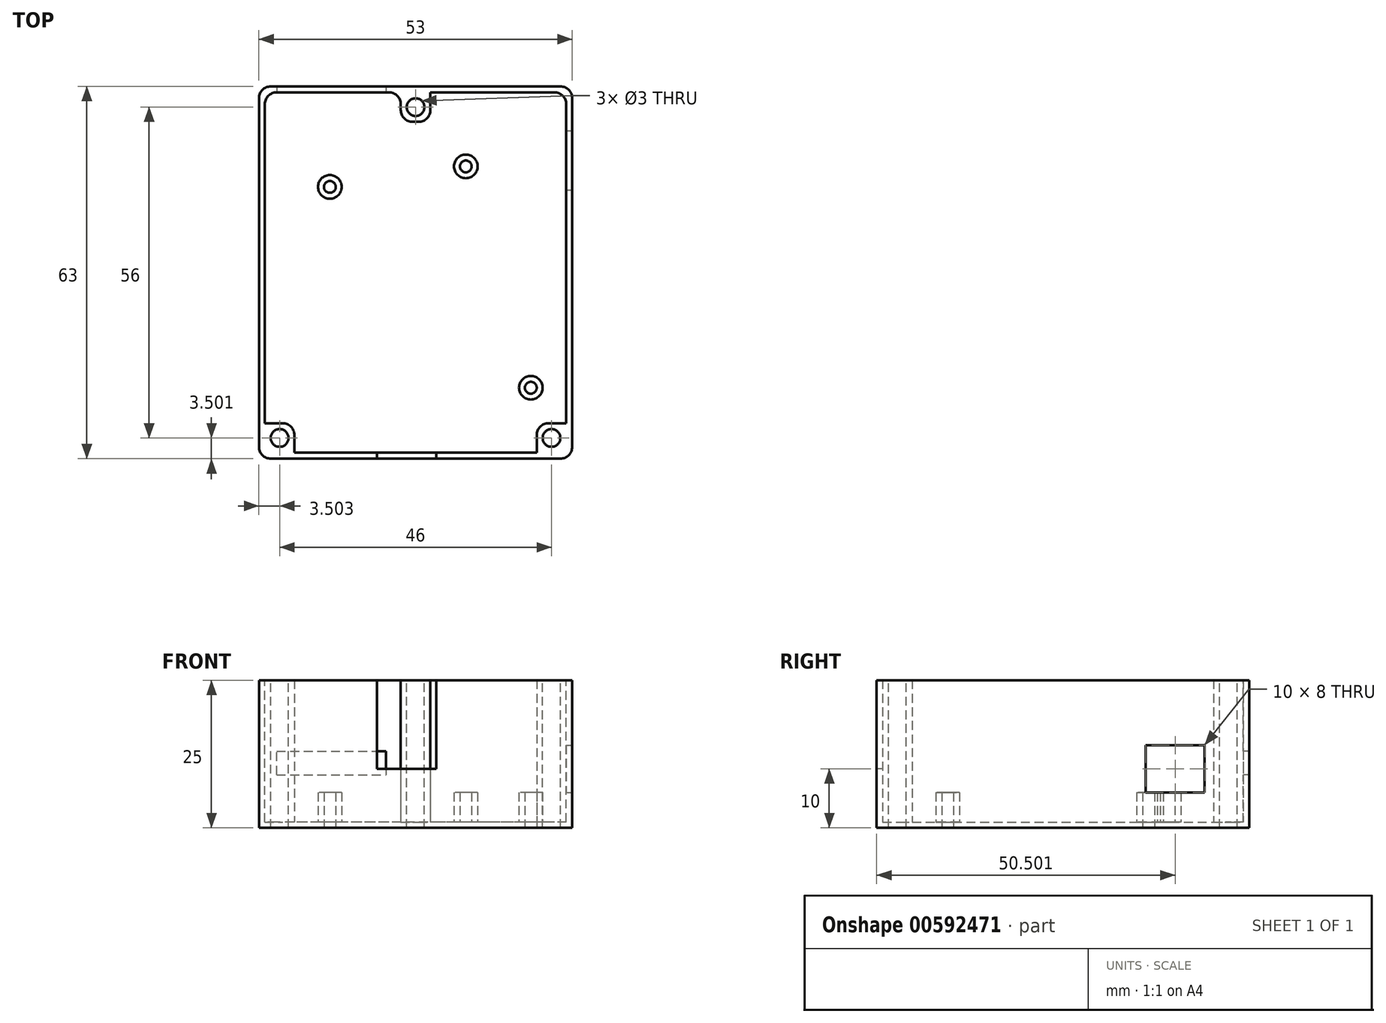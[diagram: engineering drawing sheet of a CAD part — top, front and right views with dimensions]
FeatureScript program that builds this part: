
annotation { "Feature Type Name" : "Feature", "Feature Type Description" : "" }
export const myFeature = defineFeature(function(context is Context, id is Id, definition is map)
    precondition{}
    {
        {
            var Q0;
            Q0=qCreatedBy(makeId("Top.planeOp"),FACE);
            var sketch = newSketch(context, id + "F0", { "sketchPlane" : qUnion([Q0])});
            skLineSegment(sketch, "E0.bottom", {"start": v(-63.44, 80.45) * mm, "end": v(-10.44, 80.45) * mm});
            skLineSegment(sketch, "E0.top", {"start": v(-63.44, 17.45) * mm, "end": v(-10.44, 17.45) * mm});
            skLineSegment(sketch, "E0.left", {"start": v(-63.44, 80.45) * mm, "end": v(-63.44, 17.45) * mm});
            skLineSegment(sketch, "E0.right", {"start": v(-10.44, 80.45) * mm, "end": v(-10.44, 17.45) * mm});
            skSolve(sketch);
        }
        {
            var Q0;
            Q0=makeQuery(id+"F0.imprint","IMPRINT",FACE,{"disambiguationData":[TD([[makeQuery(id+"F0.imprint","IMPRINT",EDGE,{"derivedFrom":sQuery(id+"F0.wireOp",EDGE,"E0.bottom")}),-1.0]])]});
            extrude(context, id + "F1", {"entities" : qUnion([Q0]), "depth" : 25 * mm, "offsetDistance" : 25 * mm});
        }
        {
            var Q0;
            Q0=makeQuery(id+"F1.opExtrude","CAP_FACE",FACE,{"disambiguationData":[OSD([sQuery(id+"F0.wireOp",EDGE,"E0.bottom"),sQuery(id+"F0.wireOp",EDGE,"E0.top"),sQuery(id+"F0.wireOp",EDGE,"E0.left"),sQuery(id+"F0.wireOp",EDGE,"E0.right")])],"isStart":false});
            var sketch = newSketch(context, id + "F2", { "sketchPlane" : qUnion([Q0])});
            skLineSegment(sketch, "E1.bottom", {"start": v(-11.44, 18.45) * mm, "end": v(-62.44, 18.45) * mm});
            skLineSegment(sketch, "E1.top", {"start": v(-11.44, 79.45) * mm, "end": v(-62.44, 79.45) * mm});
            skLineSegment(sketch, "E1.left", {"start": v(-11.44, 18.45) * mm, "end": v(-11.44, 79.45) * mm});
            skLineSegment(sketch, "E1.right", {"start": v(-62.44, 18.45) * mm, "end": v(-62.44, 79.45) * mm});
            skPoint(sketch, "E1.middle", {"position": v(-36.94, 48.95) * mm});
            skPoint(sketch, "E1.middle.positionSnap0", {"position": v(-63.44, 48.95) * mm});
            skPoint(sketch, "E1.middle.positionSnap1", {"position": v(-36.94, 80.45) * mm});
            skPoint(sketch, "E1.centerSnap0", {"position": v(-63.44, 48.95) * mm});
            skPoint(sketch, "E1.centerSnap1", {"position": v(-36.94, 80.45) * mm});
            skSolve(sketch);
        }
        {
            var Q0;
            Q0=makeQuery(id+"F2.imprint","IMPRINT",FACE,{"disambiguationData":[TD([[makeQuery(id+"F2.imprint","IMPRINT",EDGE,{"derivedFrom":sQuery(id+"F2.wireOp",EDGE,"E1.bottom")}),-1.0]])]});
            extrude(context, id + "F3", {"entities" : qUnion([Q0]), "operationType" : NewBodyOperationType.REMOVE, "oppositeDirection" : true, "depth" : 24 * mm, "offsetDistance" : 25 * mm});
        }
        {
            var Q0;
            Q0=makeQuery(id+"F3.boolean.opBoolean","COPY",FACE,{"derivedFrom":makeQuery(id+"F3.opExtrude","CAP_FACE",FACE,{"disambiguationData":[OSD([sQuery(id+"F2.wireOp",EDGE,"E1.bottom"),sQuery(id+"F2.wireOp",EDGE,"E1.top"),sQuery(id+"F2.wireOp",EDGE,"E1.left"),sQuery(id+"F2.wireOp",EDGE,"E1.right")])],"isStart":false})});
            var sketch = newSketch(context, id + "F4", { "sketchPlane" : qUnion([Q0])});
            skLineSegment(sketch, "E2.bottom", {"start": v(-39.44, 79.45) * mm, "end": v(-34.44, 79.45) * mm});
            skLineSegment(sketch, "E2.top", {"start": v(-39.44, 74.45) * mm, "end": v(-34.44, 74.45) * mm});
            skLineSegment(sketch, "E2.left", {"start": v(-39.44, 79.45) * mm, "end": v(-39.44, 74.45) * mm});
            skLineSegment(sketch, "E2.right", {"start": v(-34.44, 79.45) * mm, "end": v(-34.44, 74.45) * mm});
            skLineSegment(sketch, "E3.bottom", {"start": v(-62.44, 18.45) * mm, "end": v(-57.44, 18.45) * mm});
            skLineSegment(sketch, "E3.top", {"start": v(-62.44, 23.45) * mm, "end": v(-57.44, 23.45) * mm});
            skLineSegment(sketch, "E3.left", {"start": v(-62.44, 18.45) * mm, "end": v(-62.44, 23.45) * mm});
            skLineSegment(sketch, "E3.right", {"start": v(-57.44, 18.45) * mm, "end": v(-57.44, 23.45) * mm});
            skLineSegment(sketch, "E4.bottom", {"start": v(-11.44, 18.45) * mm, "end": v(-16.44, 18.45) * mm});
            skLineSegment(sketch, "E4.top", {"start": v(-11.44, 23.45) * mm, "end": v(-16.44, 23.45) * mm});
            skLineSegment(sketch, "E4.left", {"start": v(-11.44, 18.45) * mm, "end": v(-11.44, 23.45) * mm});
            skLineSegment(sketch, "E4.right", {"start": v(-16.44, 18.45) * mm, "end": v(-16.44, 23.45) * mm});
            skSolve(sketch);
        }
        {
            var Q0;
            Q0=makeQuery(id+"F4.imprint","IMPRINT",FACE,{"disambiguationData":[TD([[makeQuery(id+"F4.imprint","IMPRINT",EDGE,{"derivedFrom":sQuery(id+"F4.wireOp",EDGE,"E2.bottom")}),1.0]])]});
            var Q1;
            Q1=makeQuery(id+"F4.imprint","IMPRINT",FACE,{"disambiguationData":[TD([[makeQuery(id+"F4.imprint","IMPRINT",EDGE,{"derivedFrom":sQuery(id+"F4.wireOp",EDGE,"E3.bottom")}),-1.0]])]});
            var Q2;
            Q2=makeQuery(id+"F4.imprint","IMPRINT",FACE,{"disambiguationData":[TD([[makeQuery(id+"F4.imprint","IMPRINT",EDGE,{"derivedFrom":sQuery(id+"F4.wireOp",EDGE,"E4.bottom")}),-1.0]])]});
            extrude(context, id + "F5", {"entities" : qUnion([Q0, Q1, Q2]), "operationType" : NewBodyOperationType.ADD, "depth" : 24 * mm, "offsetDistance" : 25 * mm});
        }
        {
            var Q0;
            Q0=makeQuery(id+"F5.boolean.opBoolean","MERGE",FACE,{"derivedFrom":[makeQuery(id+"F1.opExtrude","CAP_FACE",FACE,{"disambiguationData":[OSD([sQuery(id+"F0.wireOp",EDGE,"E0.bottom"),sQuery(id+"F0.wireOp",EDGE,"E0.top"),sQuery(id+"F0.wireOp",EDGE,"E0.left"),sQuery(id+"F0.wireOp",EDGE,"E0.right")])],"isStart":false}),makeQuery(id+"F5.opExtrude","CAP_FACE",FACE,{"disambiguationData":[OSD([sQuery(id+"F4.wireOp",EDGE,"E2.bottom"),sQuery(id+"F4.wireOp",EDGE,"E2.top"),sQuery(id+"F4.wireOp",EDGE,"E2.left"),sQuery(id+"F4.wireOp",EDGE,"E2.right")])],"isStart":false}),makeQuery(id+"F5.opExtrude","CAP_FACE",FACE,{"disambiguationData":[OSD([sQuery(id+"F4.wireOp",EDGE,"E3.bottom"),sQuery(id+"F4.wireOp",EDGE,"E3.top"),sQuery(id+"F4.wireOp",EDGE,"E3.left"),sQuery(id+"F4.wireOp",EDGE,"E3.right")])],"isStart":false}),makeQuery(id+"F5.opExtrude","CAP_FACE",FACE,{"disambiguationData":[OSD([sQuery(id+"F4.wireOp",EDGE,"E4.bottom"),sQuery(id+"F4.wireOp",EDGE,"E4.top"),sQuery(id+"F4.wireOp",EDGE,"E4.left"),sQuery(id+"F4.wireOp",EDGE,"E4.right")])],"isStart":false})]});
            var sketch = newSketch(context, id + "F6", { "sketchPlane" : qUnion([Q0])});
            skCircle(sketch, "E5", {"center": v(-36.94, 76.95) * mm, "radius": 1.5 * mm});
            skPoint(sketch, "E5.centerSnap0", {"position": v(-39.44, 76.95) * mm});
            skPoint(sketch, "E5.centerSnap1", {"position": v(-36.94, 74.45) * mm});
            skCircle(sketch, "E6", {"center": v(-59.94, 20.95) * mm, "radius": 1.5 * mm});
            skPoint(sketch, "E6.centerSnap0", {"position": v(-57.44, 20.95) * mm});
            skPoint(sketch, "E6.centerSnap1", {"position": v(-59.94, 23.45) * mm});
            skCircle(sketch, "E7", {"center": v(-13.94, 20.95) * mm, "radius": 1.5 * mm});
            skPoint(sketch, "E7.centerSnap0", {"position": v(-13.94, 23.45) * mm});
            skPoint(sketch, "E7.centerSnap1", {"position": v(-16.44, 20.95) * mm});
            skSolve(sketch);
        }
        {
            var Q0;
            Q0=makeQuery(id+"F6.imprint","IMPRINT",FACE,{"disambiguationData":[TD([[makeQuery(id+"F6.imprint","IMPRINT",EDGE,{"derivedFrom":sQuery(id+"F6.wireOp",EDGE,"E5")}),1.0]])]});
            var Q1;
            Q1=makeQuery(id+"F6.imprint","IMPRINT",FACE,{"disambiguationData":[TD([[makeQuery(id+"F6.imprint","IMPRINT",EDGE,{"derivedFrom":sQuery(id+"F6.wireOp",EDGE,"E6")}),1.0]])]});
            var Q2;
            Q2=makeQuery(id+"F6.imprint","IMPRINT",FACE,{"disambiguationData":[TD([[makeQuery(id+"F6.imprint","IMPRINT",EDGE,{"derivedFrom":sQuery(id+"F6.wireOp",EDGE,"E7")}),1.0]])]});
            extrude(context, id + "F7", {"entities" : qUnion([Q0, Q1, Q2]), "operationType" : NewBodyOperationType.REMOVE, "oppositeDirection" : true, "depth" : 15 * mm, "offsetDistance" : 25 * mm});
        }
        {
            var Q0;
            Q0=makeQuery(id+"F3.boolean.opBoolean","COPY",FACE,{"derivedFrom":makeQuery(id+"F3.opExtrude","CAP_FACE",FACE,{"disambiguationData":[OSD([sQuery(id+"F2.wireOp",EDGE,"E1.bottom"),sQuery(id+"F2.wireOp",EDGE,"E1.top"),sQuery(id+"F2.wireOp",EDGE,"E1.left"),sQuery(id+"F2.wireOp",EDGE,"E1.right")])],"isStart":false})});
            var sketch = newSketch(context, id + "F8", { "sketchPlane" : qUnion([Q0])});
            skCircle(sketch, "E8", {"center": v(-51.44, 63.45) * mm, "radius": 2 * mm});
            skCircle(sketch, "E9", {"center": v(-17.44, 29.45) * mm, "radius": 2 * mm});
            skCircle(sketch, "E10", {"center": v(-51.44, 63.45) * mm, "radius": 1 * mm});
            skCircle(sketch, "E11", {"center": v(-17.44, 29.45) * mm, "radius": 1 * mm});
            skSolve(sketch);
        }
        {
            var Q0;
            Q0=makeQuery(id+"F8.imprint","IMPRINT",FACE,{"disambiguationData":[TD([[makeQuery(id+"F8.imprint","IMPRINT",EDGE,{"derivedFrom":sQuery(id+"F8.wireOp",EDGE,"E8")}),1.0]])]});
            var Q1;
            Q1=makeQuery(id+"F8.imprint","IMPRINT",FACE,{"disambiguationData":[TD([[makeQuery(id+"F8.imprint","IMPRINT",EDGE,{"derivedFrom":sQuery(id+"F8.wireOp",EDGE,"E9")}),1.0]])]});
            extrude(context, id + "F9", {"entities" : qUnion([Q0, Q1]), "operationType" : NewBodyOperationType.ADD, "depth" : 5 * mm, "offsetDistance" : 25 * mm});
        }
        {
            var Q0;
            Q0=makeQuery(id+"F9.boolean.opBoolean","SPLIT",FACE,{"disambiguationData":[TD([makeQuery(id+"F9.opExtrude","SWEPT_FACE",FACE,{"disambiguationData":[OSD([sQuery(id+"F8.wireOp",EDGE,"E10")])]})])],"derivedFrom":makeQuery(id+"F3.boolean.opBoolean","COPY",FACE,{"derivedFrom":makeQuery(id+"F3.opExtrude","CAP_FACE",FACE,{"disambiguationData":[OSD([sQuery(id+"F2.wireOp",EDGE,"E1.bottom"),sQuery(id+"F2.wireOp",EDGE,"E1.top"),sQuery(id+"F2.wireOp",EDGE,"E1.left"),sQuery(id+"F2.wireOp",EDGE,"E1.right")])],"isStart":false})})});
            var Q1;
            Q1=makeQuery(id+"F9.boolean.opBoolean","SPLIT",FACE,{"disambiguationData":[TD([makeQuery(id+"F9.opExtrude","SWEPT_FACE",FACE,{"disambiguationData":[OSD([sQuery(id+"F8.wireOp",EDGE,"E11")])]})])],"derivedFrom":makeQuery(id+"F3.boolean.opBoolean","COPY",FACE,{"derivedFrom":makeQuery(id+"F3.opExtrude","CAP_FACE",FACE,{"disambiguationData":[OSD([sQuery(id+"F2.wireOp",EDGE,"E1.bottom"),sQuery(id+"F2.wireOp",EDGE,"E1.top"),sQuery(id+"F2.wireOp",EDGE,"E1.left"),sQuery(id+"F2.wireOp",EDGE,"E1.right")])],"isStart":false})})});
            extrude(context, id + "F10", {"entities" : qUnion([Q0, Q1]), "operationType" : NewBodyOperationType.REMOVE, "oppositeDirection" : true, "depth" : 1 * mm, "offsetDistance" : 25 * mm});
        }
        {
            var Q0;
            Q0=makeQuery(id+"F1.opExtrude","SWEPT_EDGE",EDGE,{"disambiguationData":[OSD([sQuery(id+"F0.wireOp",EDGE,"E0.bottom"),sQuery(id+"F0.wireOp",EDGE,"E0.left")])]});
            var Q1;
            Q1=makeQuery(id+"F1.opExtrude","SWEPT_EDGE",EDGE,{"disambiguationData":[OSD([sQuery(id+"F0.wireOp",EDGE,"E0.bottom"),sQuery(id+"F0.wireOp",EDGE,"E0.right")])]});
            var Q2;
            Q2=makeQuery(id+"F1.opExtrude","SWEPT_EDGE",EDGE,{"disambiguationData":[OSD([sQuery(id+"F0.wireOp",EDGE,"E0.top"),sQuery(id+"F0.wireOp",EDGE,"E0.right")])]});
            var Q3;
            Q3=makeQuery(id+"F1.opExtrude","SWEPT_EDGE",EDGE,{"disambiguationData":[OSD([sQuery(id+"F0.wireOp",EDGE,"E0.top"),sQuery(id+"F0.wireOp",EDGE,"E0.left")])]});
            var Q4;
            Q4=makeQuery(id+"F5.opExtrude","SWEPT_EDGE",EDGE,{"disambiguationData":[OSD([sQuery(id+"F4.wireOp",EDGE,"E2.top"),sQuery(id+"F4.wireOp",EDGE,"E2.left")])]});
            var Q5;
            Q5=makeQuery(id+"F5.opExtrude","SWEPT_EDGE",EDGE,{"disambiguationData":[OSD([sQuery(id+"F4.wireOp",EDGE,"E2.top"),sQuery(id+"F4.wireOp",EDGE,"E2.right")])]});
            var Q6;
            Q6=makeQuery(id+"F5.opExtrude","SWEPT_EDGE",EDGE,{"disambiguationData":[OSD([sQuery(id+"F2.wireOp",EDGE,"E1.top"),sQuery(id+"F4.wireOp",EDGE,"E2.bottom"),sQuery(id+"F4.wireOp",EDGE,"E2.left")])]});
            var Q7;
            Q7=makeQuery(id+"F5.opExtrude","SWEPT_EDGE",EDGE,{"disambiguationData":[OSD([sQuery(id+"F2.wireOp",EDGE,"E1.top"),sQuery(id+"F4.wireOp",EDGE,"E2.bottom"),sQuery(id+"F4.wireOp",EDGE,"E2.right")])]});
            var Q8;
            Q8=makeQuery(id+"F5.opExtrude","SWEPT_EDGE",EDGE,{"disambiguationData":[OSD([sQuery(id+"F2.wireOp",EDGE,"E1.right"),sQuery(id+"F4.wireOp",EDGE,"E3.top"),sQuery(id+"F4.wireOp",EDGE,"E3.left")])]});
            var Q9;
            Q9=makeQuery(id+"F5.opExtrude","SWEPT_EDGE",EDGE,{"disambiguationData":[OSD([sQuery(id+"F2.wireOp",EDGE,"E1.bottom"),sQuery(id+"F4.wireOp",EDGE,"E3.bottom"),sQuery(id+"F4.wireOp",EDGE,"E3.right")])]});
            var Q10;
            Q10=makeQuery(id+"F5.opExtrude","SWEPT_EDGE",EDGE,{"disambiguationData":[OSD([sQuery(id+"F2.wireOp",EDGE,"E1.bottom"),sQuery(id+"F4.wireOp",EDGE,"E4.bottom"),sQuery(id+"F4.wireOp",EDGE,"E4.right")])]});
            var Q11;
            Q11=makeQuery(id+"F5.opExtrude","SWEPT_EDGE",EDGE,{"disambiguationData":[OSD([sQuery(id+"F2.wireOp",EDGE,"E1.left"),sQuery(id+"F4.wireOp",EDGE,"E4.top"),sQuery(id+"F4.wireOp",EDGE,"E4.left")])]});
            fillet(context, id + "F11", {"entities" : qUnion([Q0, Q1, Q2, Q3, Q4, Q5, Q6, Q7, Q8, Q9, Q10, Q11]), "radius" : 2 * mm, "tangentPropagation" : true, "allowEdgeOverflow" : false});
        }
        {
            var Q0;
            Q0=makeQuery(id+"F5.opExtrude","SWEPT_EDGE",EDGE,{"disambiguationData":[OSD([sQuery(id+"F4.wireOp",EDGE,"E3.top"),sQuery(id+"F4.wireOp",EDGE,"E3.right")])]});
            var Q1;
            Q1=makeQuery(id+"F5.opExtrude","SWEPT_EDGE",EDGE,{"disambiguationData":[OSD([sQuery(id+"F4.wireOp",EDGE,"E4.top"),sQuery(id+"F4.wireOp",EDGE,"E4.right")])]});
            fillet(context, id + "F12", {"entities" : qUnion([Q0, Q1]), "radius" : 2 * mm, "tangentPropagation" : true, "allowEdgeOverflow" : false});
        }
        {
            var Q0;
            Q0=makeQuery(id+"F3.boolean.opBoolean","COPY",EDGE,{"derivedFrom":makeQuery(id+"F3.opExtrude","SWEPT_EDGE",EDGE,{"disambiguationData":[OSD([sQuery(id+"F2.wireOp",EDGE,"E1.top"),sQuery(id+"F2.wireOp",EDGE,"E1.right")])]})});
            fillet(context, id + "F13", {"entities" : qUnion([Q0]), "radius" : 2 * mm, "tangentPropagation" : true, "allowEdgeOverflow" : false});
        }
        {
            var Q0;
            Q0=makeQuery(id+"F3.boolean.opBoolean","COPY",EDGE,{"derivedFrom":makeQuery(id+"F3.opExtrude","SWEPT_EDGE",EDGE,{"disambiguationData":[OSD([sQuery(id+"F2.wireOp",EDGE,"E1.top"),sQuery(id+"F2.wireOp",EDGE,"E1.left")])]})});
            fillet(context, id + "F14", {"entities" : qUnion([Q0]), "radius" : 2 * mm, "tangentPropagation" : true, "allowEdgeOverflow" : false});
        }
        {
            var Q0;
            {var subQ1=sQuery(id+"F2.wireOp",EDGE,"E1.right");var subQ2=sQuery(id+"F2.wireOp",EDGE,"E1.top");Q0=makeQuery(id+"F5.boolean.opBoolean","SPLIT",FACE,{"disambiguationData":[TD([makeQuery(id+"F3.boolean.opBoolean","COPY",FACE,{"derivedFrom":makeQuery(id+"F3.opExtrude","SWEPT_FACE",FACE,{"disambiguationData":[OSD([subQ1])]})})])],"derivedFrom":makeQuery(id+"F3.boolean.opBoolean","COPY",FACE,{"derivedFrom":makeQuery(id+"F3.opExtrude","SWEPT_FACE",FACE,{"disambiguationData":[OSD([subQ2])]})})});}
            var sketch = newSketch(context, id + "F15", { "sketchPlane" : qUnion([Q0])});
            skLineSegment(sketch, "E12.bottom", {"start": v(-60.46, 13) * mm, "end": v(-41.96, 13) * mm});
            skLineSegment(sketch, "E12.top", {"start": v(-60.46, 9) * mm, "end": v(-41.96, 9) * mm});
            skLineSegment(sketch, "E12.left", {"start": v(-60.46, 13) * mm, "end": v(-60.46, 9) * mm});
            skLineSegment(sketch, "E12.right", {"start": v(-41.96, 13) * mm, "end": v(-41.96, 9) * mm});
            skSolve(sketch);
        }
        {
            var Q0;
            {var subQ0=sQuery(id+"F15.wireOp",EDGE,"E12.right");Q0=makeQuery(id+"F15.imprint","IMPRINT",FACE,{"disambiguationData":[TD([[makeQuery(id+"F15.imprint","IMPRINT",EDGE,{"derivedFrom":subQ0}),-1.0]])]});}
            extrude(context, id + "F16", {"entities" : qUnion([Q0]), "operationType" : NewBodyOperationType.REMOVE, "oppositeDirection" : true, "depth" : 1 * mm, "offsetDistance" : 25 * mm});
        }
        {
            var Q0;
            Q0=makeQuery(id+"F1.opExtrude","SWEPT_FACE",FACE,{"disambiguationData":[OSD([sQuery(id+"F0.wireOp",EDGE,"E0.top")])]});
            var sketch = newSketch(context, id + "F17", { "sketchPlane" : qUnion([Q0])});
            skLineSegment(sketch, "E13.bottom", {"start": v(-43.44, 25) * mm, "end": v(-33.44, 25) * mm});
            skLineSegment(sketch, "E13.top", {"start": v(-43.44, 10) * mm, "end": v(-33.44, 10) * mm});
            skLineSegment(sketch, "E13.left", {"start": v(-43.44, 25) * mm, "end": v(-43.44, 10) * mm});
            skLineSegment(sketch, "E13.right", {"start": v(-33.44, 25) * mm, "end": v(-33.44, 10) * mm});
            skSolve(sketch);
        }
        {
            var Q0;
            Q0=makeQuery(id+"F17.imprint","IMPRINT",FACE,{"disambiguationData":[TD([[makeQuery(id+"F17.imprint","IMPRINT",EDGE,{"derivedFrom":sQuery(id+"F17.wireOp",EDGE,"E13.bottom")}),-1.0]])]});
            extrude(context, id + "F18", {"entities" : qUnion([Q0]), "operationType" : NewBodyOperationType.REMOVE, "oppositeDirection" : true, "depth" : 1 * mm, "offsetDistance" : 25 * mm});
        }
        {
            var Q0;
            Q0=makeQuery(id+"F1.opExtrude","SWEPT_FACE",FACE,{"disambiguationData":[OSD([sQuery(id+"F0.wireOp",EDGE,"E0.right")])]});
            var sketch = newSketch(context, id + "F19", { "sketchPlane" : qUnion([Q0])});
            skLineSegment(sketch, "E14.bottom", {"start": v(72.95, 14) * mm, "end": v(62.95, 14) * mm});
            skLineSegment(sketch, "E14.top", {"start": v(72.95, 6) * mm, "end": v(62.95, 6) * mm});
            skLineSegment(sketch, "E14.left", {"start": v(72.95, 14) * mm, "end": v(72.95, 6) * mm});
            skLineSegment(sketch, "E14.right", {"start": v(62.95, 14) * mm, "end": v(62.95, 6) * mm});
            skSolve(sketch);
        }
        {
            var Q0;
            Q0=makeQuery(id+"F19.imprint","IMPRINT",FACE,{"disambiguationData":[TD([[makeQuery(id+"F19.imprint","IMPRINT",EDGE,{"derivedFrom":sQuery(id+"F19.wireOp",EDGE,"E14.bottom")}),1.0]])]});
            extrude(context, id + "F20", {"entities" : qUnion([Q0]), "operationType" : NewBodyOperationType.REMOVE, "oppositeDirection" : true, "depth" : 1 * mm, "offsetDistance" : 25 * mm});
        }
        {
            var Q0;
            Q0=makeQuery(id+"F7.boolean.opBoolean","COPY",FACE,{"derivedFrom":makeQuery(id+"F7.opExtrude","CAP_FACE",FACE,{"disambiguationData":[OSD([sQuery(id+"F6.wireOp",EDGE,"E6")])],"isStart":false})});
            var Q1;
            Q1=makeQuery(id+"F7.boolean.opBoolean","COPY",FACE,{"derivedFrom":makeQuery(id+"F7.opExtrude","CAP_FACE",FACE,{"disambiguationData":[OSD([sQuery(id+"F6.wireOp",EDGE,"E7")])],"isStart":false})});
            var Q2;
            Q2=makeQuery(id+"F7.boolean.opBoolean","COPY",FACE,{"derivedFrom":makeQuery(id+"F7.opExtrude","CAP_FACE",FACE,{"disambiguationData":[OSD([sQuery(id+"F6.wireOp",EDGE,"E5")])],"isStart":false})});
            extrude(context, id + "F21", {"entities" : qUnion([Q0, Q1, Q2]), "operationType" : NewBodyOperationType.REMOVE, "oppositeDirection" : true, "depth" : 15 * mm, "offsetDistance" : 25 * mm});
        }
        {
            var Q0;
            {var subQ0=sQuery(id+"F2.wireOp",EDGE,"E1.bottom");var subQ1=sQuery(id+"F2.wireOp",EDGE,"E1.top");var subQ2=sQuery(id+"F2.wireOp",EDGE,"E1.left");var subQ3=sQuery(id+"F2.wireOp",EDGE,"E1.right");Q0=makeQuery(id+"F9.boolean.opBoolean","SPLIT",FACE,{"disambiguationData":[TD([makeQuery(id+"F3.boolean.opBoolean","COPY",FACE,{"derivedFrom":makeQuery(id+"F3.opExtrude","SWEPT_FACE",FACE,{"disambiguationData":[OSD([subQ0])]})})])],"derivedFrom":makeQuery(id+"F3.boolean.opBoolean","COPY",FACE,{"derivedFrom":makeQuery(id+"F3.opExtrude","CAP_FACE",FACE,{"disambiguationData":[OSD([subQ0,subQ1,subQ2,subQ3])],"isStart":false})})});}
            var sketch = newSketch(context, id + "F22", { "sketchPlane" : qUnion([Q0])});
            skCircle(sketch, "E15", {"center": v(-28.44, 66.92) * mm, "radius": 2 * mm});
            skCircle(sketch, "E16", {"center": v(-28.44, 66.92) * mm, "radius": 1 * mm});
            skSolve(sketch);
        }
        {
            var Q0;
            Q0=makeQuery(id+"F22.imprint","IMPRINT",FACE,{"disambiguationData":[TD([[makeQuery(id+"F22.imprint","IMPRINT",EDGE,{"derivedFrom":sQuery(id+"F22.wireOp",EDGE,"E15")}),1.0]])]});
            extrude(context, id + "F23", {"entities" : qUnion([Q0]), "operationType" : NewBodyOperationType.ADD, "depth" : 5 * mm, "offsetDistance" : 25 * mm});
        }
    });
